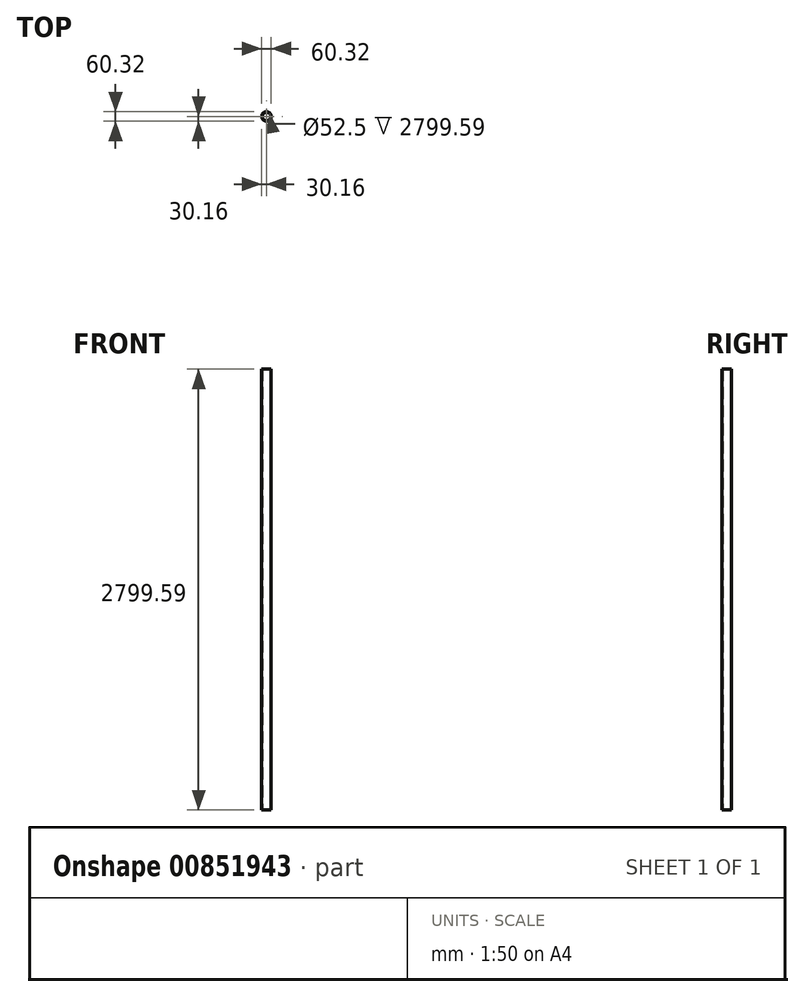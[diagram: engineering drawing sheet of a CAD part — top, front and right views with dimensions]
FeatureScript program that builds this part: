
annotation { "Feature Type Name" : "Feature", "Feature Type Description" : "" }
export const myFeature = defineFeature(function(context is Context, id is Id, definition is map)
    precondition{}
    {
        {
            var Q0;
            Q0=qCreatedBy(makeId("Top.planeOp"),FACE);
            var sketch = newSketch(context, id + "F0", { "sketchPlane" : qUnion([Q0])});
            skCircle(sketch, "E0", {"center": v(0, 0) * mm, "radius": 30.16 * mm});
            skCircle(sketch, "E1", {"center": v(0, 0) * mm, "radius": 26.25 * mm});
            skSolve(sketch);
        }
        {
            var Q0;
            Q0=qSketchRegion(id+"F0",true);
            extrude(context, id + "F1", {"entities" : qUnion([Q0]), "depth" : 2799.6 * mm, "offsetDistance" : 25.4 * mm});
        }
    });
